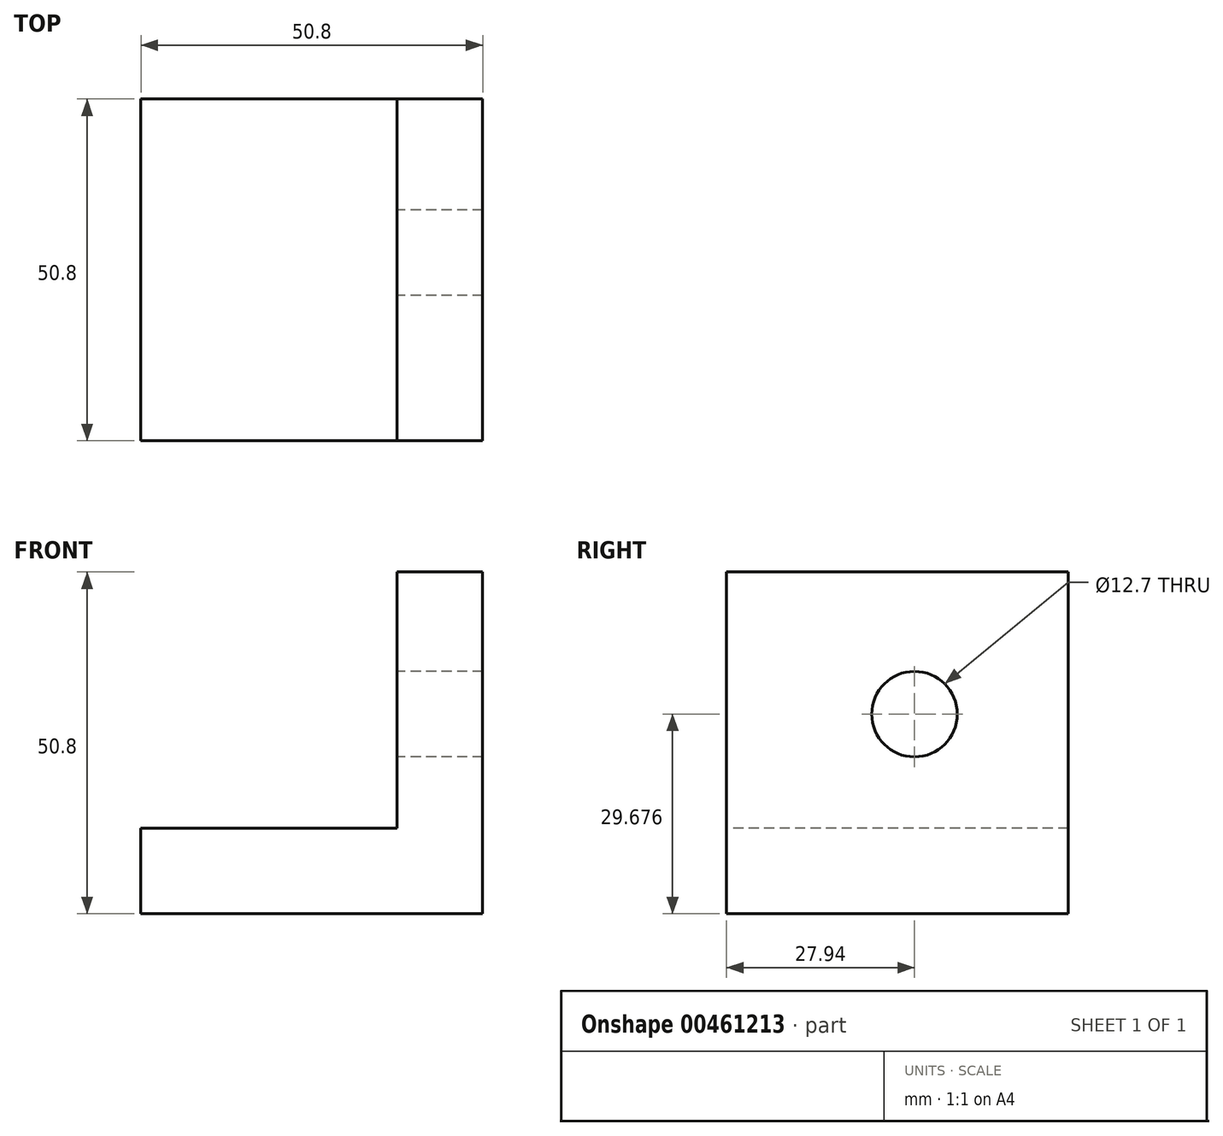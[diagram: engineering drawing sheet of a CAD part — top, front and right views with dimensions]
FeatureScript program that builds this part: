
annotation { "Feature Type Name" : "Feature", "Feature Type Description" : "" }
export const myFeature = defineFeature(function(context is Context, id is Id, definition is map)
    precondition{}
    {
        {
            var Q0;
            Q0=qCreatedBy(makeId("Front.planeOp"),FACE);
            var sketch = newSketch(context, id + "F0", { "sketchPlane" : qUnion([Q0])});
            skLineSegment(sketch, "E0.bottom", {"start": v(-7.43, 50.8) * mm, "end": v(5.27, 50.8) * mm});
            skLineSegment(sketch, "E0.top", {"start": v(-7.43, 0) * mm, "end": v(5.27, 0) * mm});
            skLineSegment(sketch, "E0.left", {"start": v(-7.43, 50.8) * mm, "end": v(-7.43, 0) * mm});
            skLineSegment(sketch, "E0.right", {"start": v(5.27, 50.8) * mm, "end": v(5.27, 0) * mm});
            skSolve(sketch);
        }
        {
            var Q0;
            Q0 = qSketchRegion(id + "F0", true);
            extrude(context, id + "F1", {"entities" : qUnion([Q0]), "depth" : 50.8 * mm});
        }
        {
            var Q0;
            Q0=makeQuery(id+"F1.opExtrude","SWEPT_FACE",FACE,{"disambiguationData":[OSD([sQuery(id+"F0.wireOp",EDGE,"E0.left")])]});
            var sketch = newSketch(context, id + "F2", { "sketchPlane" : qUnion([Q0])});
            skLineSegment(sketch, "E1", {"start": v(0, 0) * mm, "end": v(0, 12.7) * mm});
            skLineSegment(sketch, "E2", {"start": v(0, 12.7) * mm, "end": v(50.8, 12.7) * mm});
            skSolve(sketch);
        }
        {
            var Q0;
            Q0 = qSketchRegion(id + "F2", true);
            var Q1;
            Q1=makeQuery(id+"F2.imprint","IMPRINT",FACE,{"disambiguationData":[TD([[makeQuery(id+"F2.imprint","IMPRINT",EDGE,{"derivedFrom":sQuery(id+"F2.wireOp",EDGE,"E1")}),1.0]])]});
            extrude(context, id + "F3", {"entities" : qUnion([Q0, Q1]), "operationType" : NewBodyOperationType.ADD, "depth" : 38.1 * mm});
        }
        {
            var Q0;
            Q0=makeQuery(id+"F1.opExtrude","SWEPT_FACE",FACE,{"disambiguationData":[OSD([sQuery(id+"F0.wireOp",EDGE,"E0.left")])]});
            var sketch = newSketch(context, id + "F4", { "sketchPlane" : qUnion([Q0])});
            skCircle(sketch, "E3", {"center": v(22.86, 29.68) * mm, "radius": 6.35 * mm});
            skSolve(sketch);
        }
        {
            var Q0;
            Q0 = qSketchRegion(id + "F4", true);
            extrude(context, id + "F5", {"entities" : qUnion([Q0]), "operationType" : NewBodyOperationType.REMOVE, "oppositeDirection" : true, "depth" : 25.4 * mm});
        }
    });
